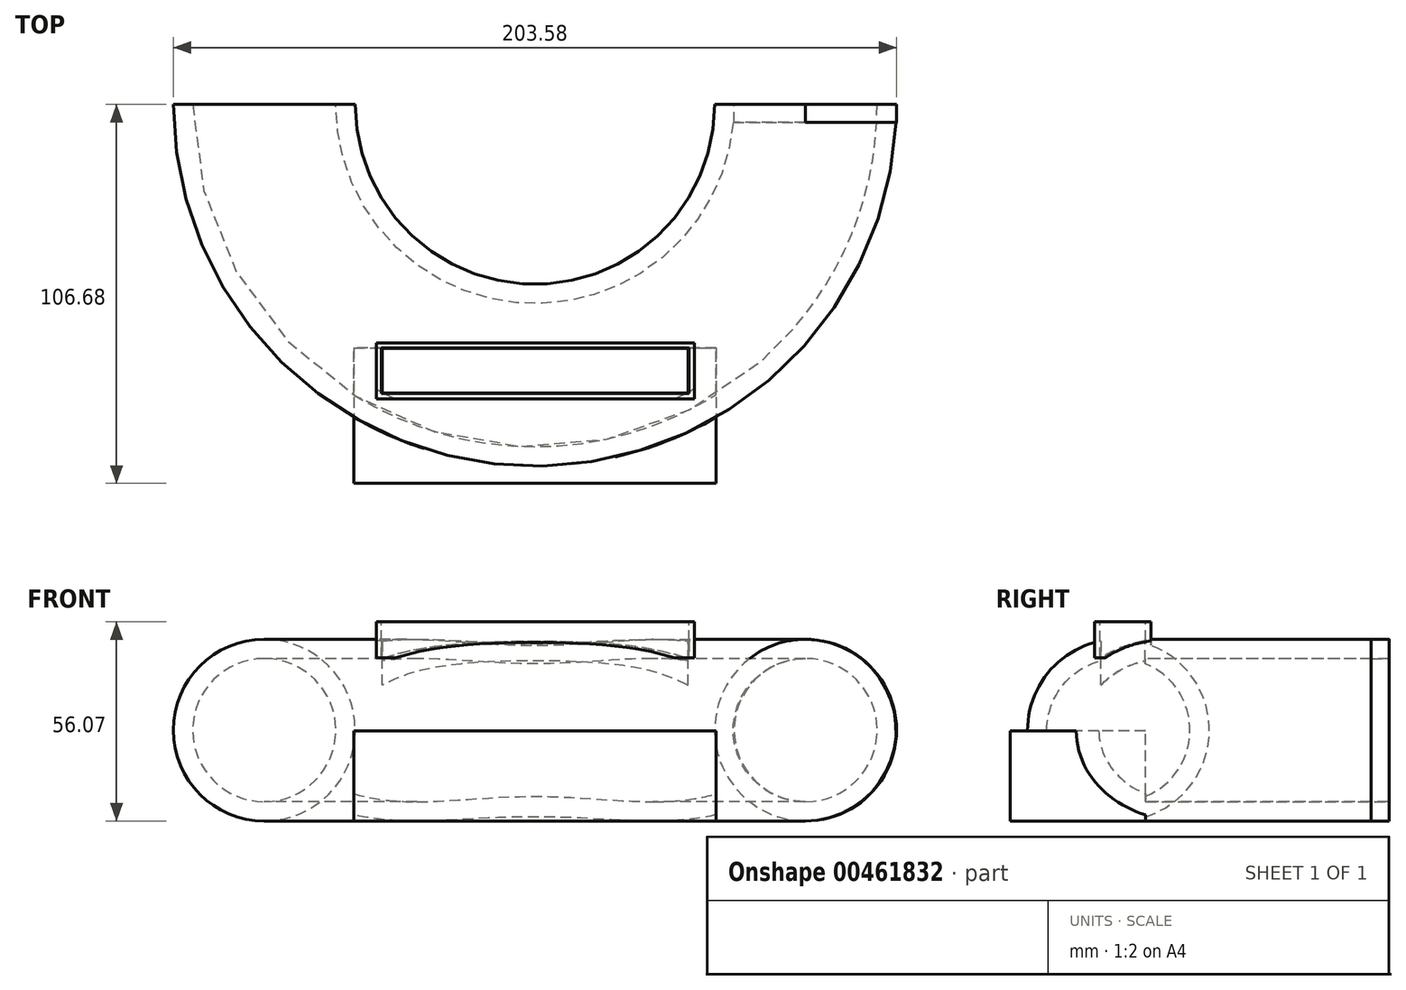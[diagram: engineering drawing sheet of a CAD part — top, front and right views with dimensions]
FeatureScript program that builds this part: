
annotation { "Feature Type Name" : "Feature", "Feature Type Description" : "" }
export const myFeature = defineFeature(function(context is Context, id is Id, definition is map)
    precondition{}
    {
        {
            var Q0;
            Q0=qCreatedBy(makeId("Front.planeOp"),FACE);
            var sketch = newSketch(context, id + "F0", { "sketchPlane" : qUnion([Q0])});
            skCircle(sketch, "E0", {"center": v(0, 0) * mm, "radius": 25.59 * mm});
            skCircle(sketch, "E1", {"center": v(0, 0) * mm, "radius": 20.14 * mm});
            skSolve(sketch);
        }
        {
            var Q0;
            Q0=qCreatedBy(makeId("Top.planeOp"),FACE);
            var sketch = newSketch(context, id + "F1", { "sketchPlane" : qUnion([Q0])});
            skArc(sketch, "E2", {"start": v(-152.4, 0) * mm, "mid": v(-76.2, -76.2) * mm, "end": v(0, 0) * mm});
            skSolve(sketch);
        }
        {
            var Q0;
            Q0=makeQuery(id+"F0.imprint","IMPRINT",FACE,{"disambiguationData":[TD([[makeQuery(id+"F0.imprint","IMPRINT",EDGE,{"derivedFrom":sQuery(id+"F0.wireOp",EDGE,"E0")}),1.0]])]});
            extrude(context, id + "F2", {"entities" : qUnion([Q0]), "depth" : 5.08 * mm});
        }
        {
            var Q0;
            Q0=makeQuery(id+"F0.imprint","IMPRINT",FACE,{"disambiguationData":[TD([[makeQuery(id+"F0.imprint","IMPRINT",EDGE,{"derivedFrom":sQuery(id+"F0.wireOp",EDGE,"E0")}),1.0]])]});
            var Q1;
            Q1=sQuery(id+"F1.wireOp",EDGE,"E2");
            sweep(context, id + "F3", {"operationType" : NewBodyOperationType.ADD, "profiles" : qUnion([Q0]), "path" : qUnion([Q1])});
        }
        {
            var Q0;
            Q0=qCreatedBy(makeId("Top.planeOp"),FACE);
            cPlane(context, id + "F4", {"entities" : qUnion([Q0]), "cplaneType" : CPlaneType.OFFSET, "offset" : 30.48 * mm, "width" : 152.4 * mm, "height" : 152.4 * mm});
        }
        {
            var Q0;
            Q0=qCreatedBy(makeId("Front.planeOp"),FACE);
            cPlane(context, id + "F5", {"entities" : qUnion([Q0]), "cplaneType" : CPlaneType.OFFSET, "offset" : 106.68 * mm, "width" : 152.4 * mm, "height" : 152.4 * mm});
        }
        {
            var Q0;
            Q0=qCreatedBy(id+"F5.planeOp",FACE);
            var sketch = newSketch(context, id + "F6", { "sketchPlane" : qUnion([Q0])});
            skLineSegment(sketch, "E3.bottom", {"start": v(-127.19, -25.59) * mm, "end": v(-25.21, -25.59) * mm});
            skLineSegment(sketch, "E3.top", {"start": v(-127.19, -0.19) * mm, "end": v(-25.21, -0.19) * mm});
            skLineSegment(sketch, "E3.left", {"start": v(-127.19, -25.59) * mm, "end": v(-127.19, -0.19) * mm});
            skLineSegment(sketch, "E3.right", {"start": v(-25.21, -25.59) * mm, "end": v(-25.21, -0.19) * mm});
            skSolve(sketch);
        }
        {
            var Q0;
            Q0=makeQuery(id+"F6.imprint","IMPRINT",FACE,{"disambiguationData":[TD([[makeQuery(id+"F6.imprint","IMPRINT",EDGE,{"derivedFrom":sQuery(id+"F6.wireOp",EDGE,"E3.bottom")}),1.0]])]});
            extrude(context, id + "F7", {"entities" : qUnion([Q0]), "operationType" : NewBodyOperationType.ADD, "oppositeDirection" : true, "depth" : 38.1 * mm});
        }
        {
            var Q0;
            Q0=qCreatedBy(id+"F4.planeOp",FACE);
            var sketch = newSketch(context, id + "F8", { "sketchPlane" : qUnion([Q0])});
            skLineSegment(sketch, "E4.bottom", {"start": v(-119.42, -68.53) * mm, "end": v(-32.86, -68.53) * mm});
            skLineSegment(sketch, "E4.top", {"start": v(-119.42, -81.35) * mm, "end": v(-32.86, -81.35) * mm});
            skLineSegment(sketch, "E4.left", {"start": v(-119.42, -68.53) * mm, "end": v(-119.42, -81.35) * mm});
            skLineSegment(sketch, "E4.right", {"start": v(-32.86, -68.53) * mm, "end": v(-32.86, -81.35) * mm});
            skLineSegment(sketch, "E5.bottom", {"start": v(-120.82, -67.1) * mm, "end": v(-31.29, -67.1) * mm});
            skLineSegment(sketch, "E5.top", {"start": v(-120.82, -82.88) * mm, "end": v(-31.29, -82.88) * mm});
            skLineSegment(sketch, "E5.left", {"start": v(-120.82, -67.1) * mm, "end": v(-120.82, -82.88) * mm});
            skLineSegment(sketch, "E5.right", {"start": v(-31.29, -67.1) * mm, "end": v(-31.29, -82.88) * mm});
            skSolve(sketch);
        }
        {
            var Q0;
            Q0=makeQuery(id+"F8.imprint","IMPRINT",FACE,{"disambiguationData":[TD([[makeQuery(id+"F8.imprint","IMPRINT",EDGE,{"derivedFrom":sQuery(id+"F8.wireOp",EDGE,"E4.bottom")}),1.0]])]});
            extrude(context, id + "F9", {"entities" : qUnion([Q0]), "operationType" : NewBodyOperationType.ADD, "oppositeDirection" : true, "depth" : 10.16 * mm});
        }
        {
            var Q0;
            Q0=qCreatedBy(makeId("Top.planeOp"),FACE);
            cPlane(context, id + "F10", {"entities" : qUnion([Q0]), "cplaneType" : CPlaneType.OFFSET, "offset" : 25.4 * mm, "oppositeDirection" : true, "width" : 152.4 * mm, "height" : 152.4 * mm});
        }
        {
            var Q0;
            Q0=qCreatedBy(id+"F10.planeOp",FACE);
            var sketch = newSketch(context, id + "F11", { "sketchPlane" : qUnion([Q0])});
            skLineSegment(sketch, "E6.bottom", {"start": v(-82.72, -69.53) * mm, "end": v(-70, -69.53) * mm});
            skLineSegment(sketch, "E6.top", {"start": v(-82.72, -80.62) * mm, "end": v(-70, -80.62) * mm});
            skLineSegment(sketch, "E6.left", {"start": v(-82.72, -69.53) * mm, "end": v(-82.72, -80.62) * mm});
            skLineSegment(sketch, "E6.right", {"start": v(-70, -69.53) * mm, "end": v(-70, -80.62) * mm});
            skSolve(sketch);
        }
        {
            var Q0;
            Q0 = qSketchRegion(id + "F11", true);
            extrude(context, id + "F12", {"entities" : qUnion([Q0]), "operationType" : NewBodyOperationType.ADD, "depth" : 10.16 * mm});
        }
        {
            var Q0;
            Q0=qCreatedBy(id+"F4.planeOp",FACE);
            var sketch = newSketch(context, id + "F13", { "sketchPlane" : qUnion([Q0])});
            skLineSegment(sketch, "E7.bottom", {"start": v(-119.24, -68.69) * mm, "end": v(-33.02, -68.69) * mm});
            skLineSegment(sketch, "E7.top", {"start": v(-119.24, -81.2) * mm, "end": v(-33.02, -81.2) * mm});
            skLineSegment(sketch, "E7.left", {"start": v(-119.24, -68.69) * mm, "end": v(-119.24, -81.2) * mm});
            skLineSegment(sketch, "E7.right", {"start": v(-33.02, -68.69) * mm, "end": v(-33.02, -81.2) * mm});
            skSolve(sketch);
        }
        {
            var Q0;
            Q0 = qSketchRegion(id + "F13", true);
            extrude(context, id + "F14", {"entities" : qUnion([Q0]), "operationType" : NewBodyOperationType.REMOVE, "oppositeDirection" : true, "depth" : 17.78 * mm});
        }
    });
